# Revit family: Qf_Marco_1000830_SP9_Head
name_source: partatom
category: Specialty Equipment
units: mm (PartAtom-declared; Revit-internal decimal feet)

## family parameters
Always vertical = Yes
Cut with Voids When Loaded = No
Part Type = Normal
Room Calculation Point = No
Round Connector Dimension = Use Diameter
Shared = No
Work Plane-Based = No

## types (1)
- Qf_Marco_1000830_SP9_Head
    Apparent Power = 0 VA
    Conn Conduit = Yes
    Cycle = 0 Hz
    Depth = 7.59 "
    Description = Marco SP9 Head To Be Used With The SP9 Undercounter Water Boiler.
    Elec Conn Connection Height = 0 "
    Elec Conn RI Height = 0 "
    FL Amps = 0 A
    Foodservice Equipment Identifier = Yes
    Height = 16.39 "
    Identify Quantity as Lot = Yes
    Length = 5.16 "
    Manufacturer = Marco Beverage Systems Ltd.
    Max Overcurrent Protection = 0 A
    Min Ckt Ampacity = 0 A
    Model = 1000830
    Number of Poles = 1
    Phase = 0
    Volts = 0 V
    Watts = 0 W
    Weight in Pounds = 0

## geometry (parser evidence)
native form markers: Sweep x6
no freeform markers — native parametric forms only
